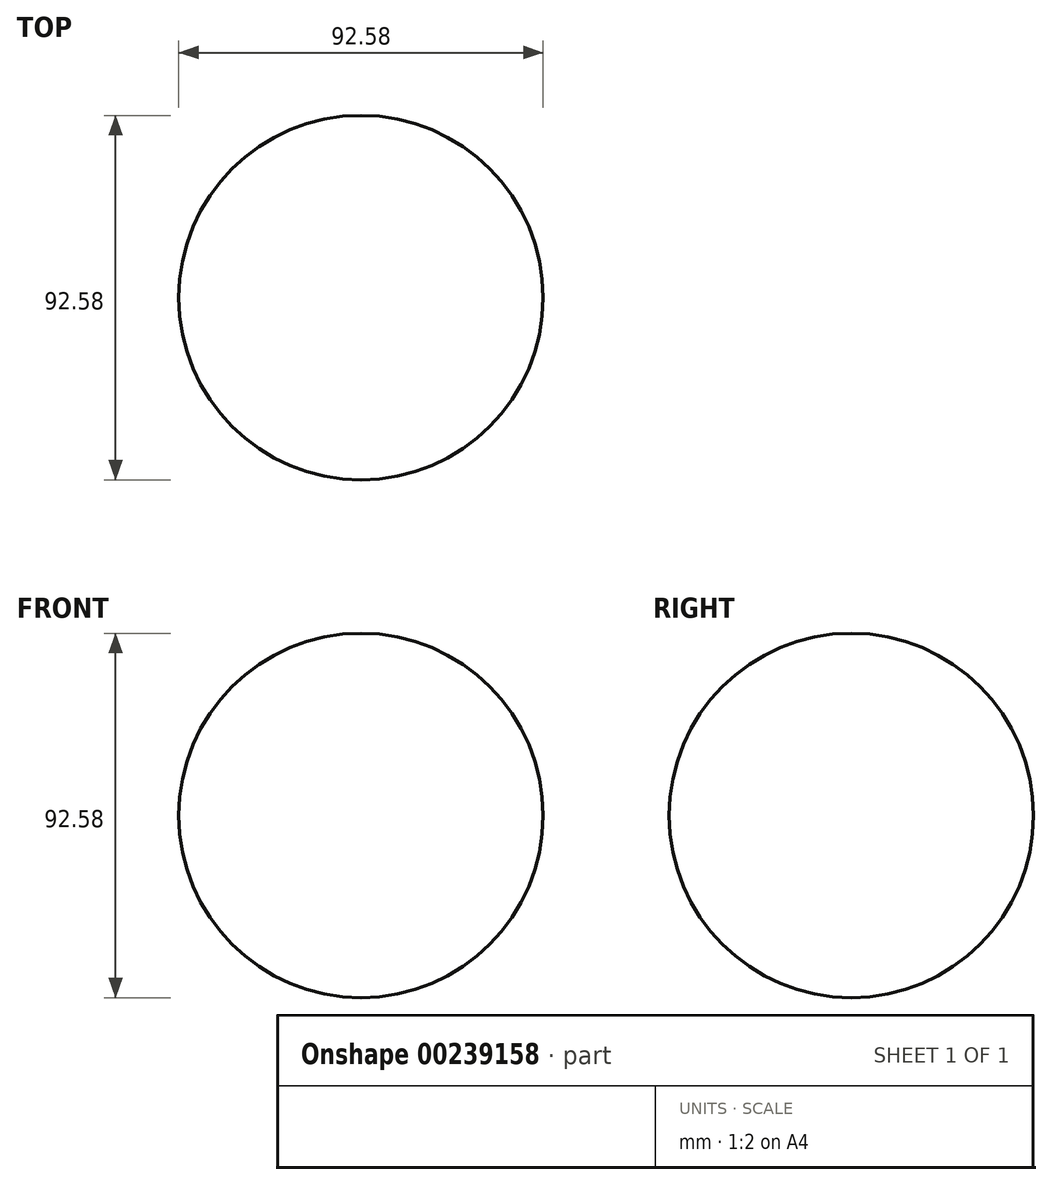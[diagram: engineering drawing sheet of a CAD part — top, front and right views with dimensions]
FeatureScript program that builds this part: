
annotation { "Feature Type Name" : "Feature", "Feature Type Description" : "" }
export const myFeature = defineFeature(function(context is Context, id is Id, definition is map)
    precondition{}
    {
        {
            var Q0;
            Q0=qCreatedBy(makeId("Front.planeOp"),FACE);
            var sketch = newSketch(context, id + "F0", { "sketchPlane" : qUnion([Q0])});
            skArc(sketch, "E0", {"start": v(0, -46.3) * mm, "mid": v(46.3, 0) * mm, "end": v(0, 46.3) * mm});
            skLineSegment(sketch, "E1", {"start": v(0, 46.3) * mm, "end": v(0, -46.3) * mm});
            skSolve(sketch);
        }
        {
            var Q0;
            Q0=makeQuery(id+"F0.imprint","IMPRINT",FACE,{"disambiguationData":[TD([[makeQuery(id+"F0.imprint","IMPRINT",EDGE,{"derivedFrom":sQuery(id+"F0.wireOp",EDGE,"E0")}),1.0]])]});
            var Q1;
            Q1=sQuery(id+"F0.wireOp",EDGE,"E1");
            revolve(context, id + "F1", {"entities" : qUnion([Q0]), "axis" : qUnion([Q1]), "revolveType" : RevolveType.FULL});
        }
    });
